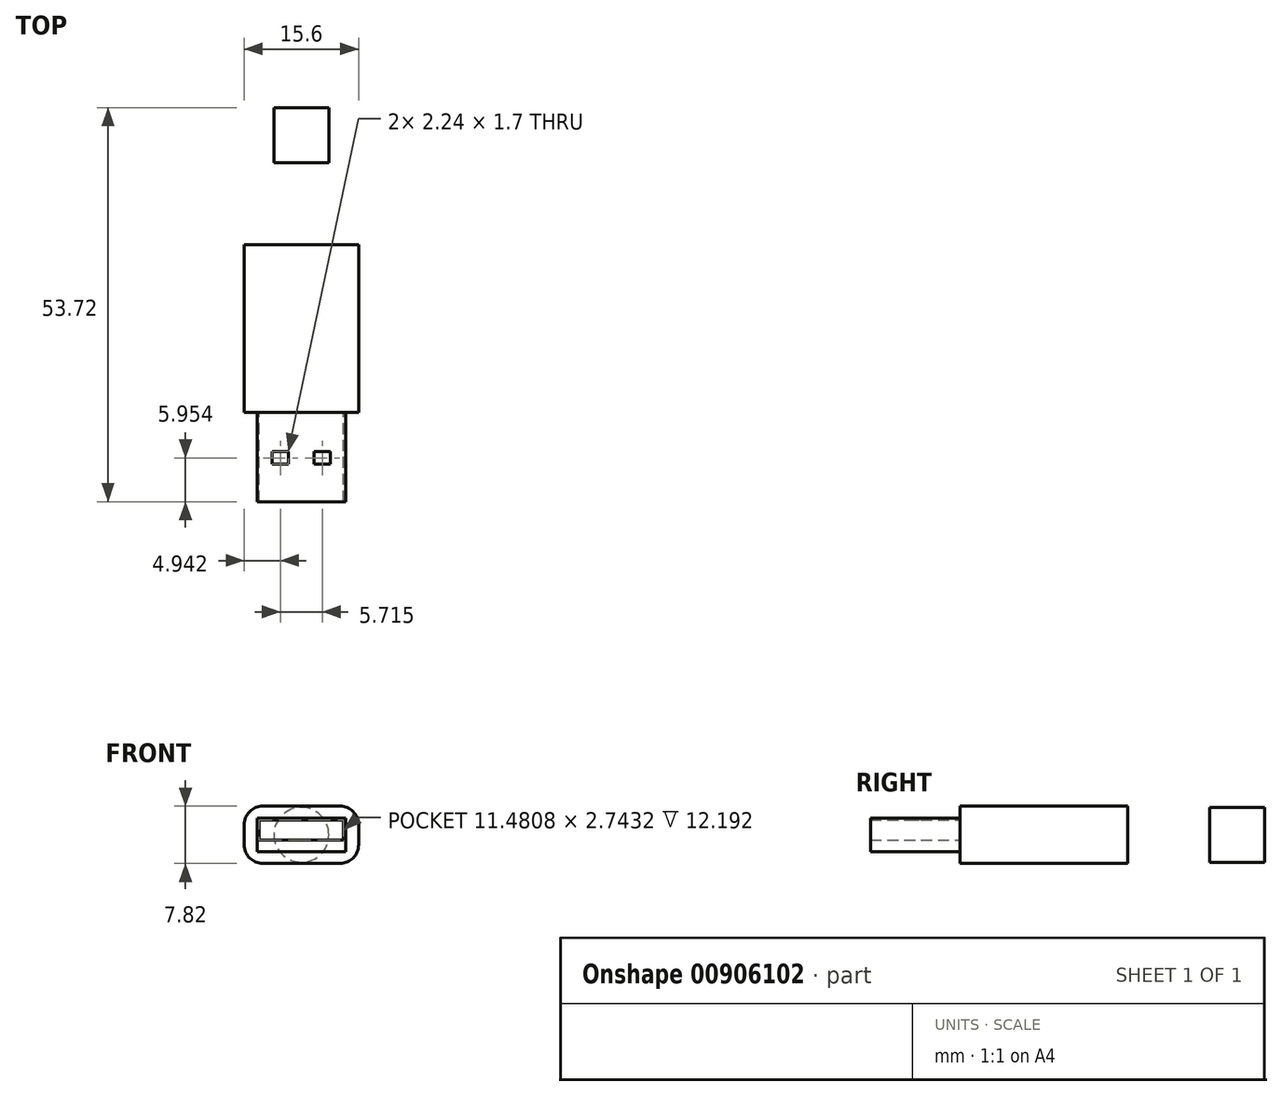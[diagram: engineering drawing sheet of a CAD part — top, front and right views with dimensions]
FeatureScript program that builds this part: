
annotation { "Feature Type Name" : "Feature", "Feature Type Description" : "" }
export const myFeature = defineFeature(function(context is Context, id is Id, definition is map)
    precondition{}
    {
        {
            var Q0;
            Q0=qCreatedBy(makeId("Front.planeOp"),FACE);
            var sketch = newSketch(context, id + "F0", { "sketchPlane" : qUnion([Q0])});
            skLineSegment(sketch, "E0.bottom", {"start": v(6.02, -2.29) * mm, "end": v(-6.02, -2.29) * mm});
            skLineSegment(sketch, "E0.top", {"start": v(6.02, 2.29) * mm, "end": v(-6.02, 2.29) * mm});
            skLineSegment(sketch, "E0.left", {"start": v(6.02, -2.29) * mm, "end": v(6.02, 2.29) * mm});
            skLineSegment(sketch, "E0.right", {"start": v(-6.02, -2.29) * mm, "end": v(-6.02, 2.29) * mm});
            skPoint(sketch, "E0.middle", {"position": v(0, 0) * mm});
            skSolve(sketch);
        }
        {
            var Q0;
            Q0=qSketchRegion(id+"F0",true);
            extrude(context, id + "F1", {"entities" : qUnion([Q0]), "depth" : 12.2 * mm, "offsetDistance" : 25.4 * mm});
        }
        {
            var Q0;
            Q0=makeQuery(id+"F1.opExtrude","CAP_FACE",FACE,{"disambiguationData":[OSD([sQuery(id+"F0.wireOp",EDGE,"E0.bottom"),sQuery(id+"F0.wireOp",EDGE,"E0.top"),sQuery(id+"F0.wireOp",EDGE,"E0.left"),sQuery(id+"F0.wireOp",EDGE,"E0.right")])],"isStart":false});
            var Q1;
            Q1=makeQuery(id+"F1.opExtrude","CAP_FACE",FACE,{"disambiguationData":[OSD([sQuery(id+"F0.wireOp",EDGE,"E0.bottom"),sQuery(id+"F0.wireOp",EDGE,"E0.top"),sQuery(id+"F0.wireOp",EDGE,"E0.left"),sQuery(id+"F0.wireOp",EDGE,"E0.right")])],"isStart":true});
            shell(context, id + "F2", {"entities" : qUnion([Q0, Q1]), "thickness" : 0.28 * mm});
        }
        {
            var Q0;
            Q0=qCreatedBy(makeId("Front.planeOp"),FACE);
            var sketch = newSketch(context, id + "F3", { "sketchPlane" : qUnion([Q0])});
            skLineSegment(sketch, "E1.bottom", {"start": v(5.26, 3.91) * mm, "end": v(-5.26, 3.91) * mm});
            skLineSegment(sketch, "E1.top", {"start": v(5.26, -3.91) * mm, "end": v(-5.26, -3.91) * mm});
            skLineSegment(sketch, "E1.left", {"start": v(7.8, 1.37) * mm, "end": v(7.8, -1.37) * mm});
            skLineSegment(sketch, "E1.right", {"start": v(-7.8, 1.37) * mm, "end": v(-7.8, -1.37) * mm});
            skPoint(sketch, "E1.middle", {"position": v(0, 0) * mm});
            skPoint(sketch, "E2.visualSharp", {"position": v(-7.8, 3.91) * mm});
            skArc(sketch, "E2.filletArc", {"start": v(-5.26, 3.91) * mm, "mid": v(-7.05, 3.17) * mm, "end": v(-7.8, 1.37) * mm});
            skPoint(sketch, "E3.visualSharp", {"position": v(7.8, 3.91) * mm});
            skArc(sketch, "E3.filletArc", {"start": v(7.8, 1.37) * mm, "mid": v(7.05, 3.17) * mm, "end": v(5.26, 3.91) * mm});
            skPoint(sketch, "E4.visualSharp", {"position": v(7.8, -3.91) * mm});
            skArc(sketch, "E4.filletArc", {"start": v(5.26, -3.91) * mm, "mid": v(7.05, -3.17) * mm, "end": v(7.8, -1.37) * mm});
            skPoint(sketch, "E5.visualSharp", {"position": v(-7.8, -3.91) * mm});
            skArc(sketch, "E5.filletArc", {"start": v(-7.8, -1.37) * mm, "mid": v(-7.05, -3.17) * mm, "end": v(-5.26, -3.91) * mm});
            skSolve(sketch);
        }
        {
            var Q0;
            Q0=qSketchRegion(id+"F3",true);
            extrude(context, id + "F4", {"entities" : qUnion([Q0]), "operationType" : NewBodyOperationType.ADD, "oppositeDirection" : true, "depth" : 22.86 * mm, "offsetDistance" : 25.4 * mm});
        }
        {
            var Q0;
            Q0=makeQuery(id+"F2.opShell","OFFSET_FACE",FACE,{"disambiguationData":[OSD([sQuery(id+"F0.wireOp",EDGE,"E0.bottom")])]});
            var sketch = newSketch(context, id + "F5", { "sketchPlane" : qUnion([Q0])});
            skLineSegment(sketch, "E6.0", {"start": v(-5.74, -12.2) * mm, "end": v(-5.74, 0) * mm});
            skLineSegment(sketch, "E6.1", {"start": v(5.74, 0) * mm, "end": v(-5.74, 0) * mm});
            skLineSegment(sketch, "E6.2", {"start": v(5.74, -12.2) * mm, "end": v(5.74, 0) * mm});
            skLineSegment(sketch, "E6.3", {"start": v(5.74, -12.2) * mm, "end": v(-5.74, -12.2) * mm});
            skSolve(sketch);
        }
        {
            var Q0;
            Q0=makeQuery(id+"F5.imprint","IMPRINT",FACE,{"disambiguationData":[TD([[makeQuery(id+"F5.imprint","IMPRINT",EDGE,{"derivedFrom":sQuery(id+"F5.wireOp",EDGE,"E6.0")}),-1.0]])]});
            extrude(context, id + "F6", {"entities" : qUnion([Q0]), "operationType" : NewBodyOperationType.ADD, "depth" : 1.27 * mm, "offsetDistance" : 25.4 * mm});
        }
        {
            var Q0;
            Q0=makeQuery(id+"F1.opExtrude","SWEPT_FACE",FACE,{"disambiguationData":[OSD([sQuery(id+"F0.wireOp",EDGE,"E0.top")])]});
            var sketch = newSketch(context, id + "F7", { "sketchPlane" : qUnion([Q0])});
            skLineSegment(sketch, "E7.bottom", {"start": v(-1.74, -7.09) * mm, "end": v(-3.98, -7.09) * mm});
            skLineSegment(sketch, "E7.top", {"start": v(-1.74, -5.38) * mm, "end": v(-3.98, -5.38) * mm});
            skLineSegment(sketch, "E7.left", {"start": v(-1.74, -7.09) * mm, "end": v(-1.74, -5.38) * mm});
            skLineSegment(sketch, "E7.right", {"start": v(-3.98, -7.09) * mm, "end": v(-3.98, -5.38) * mm});
            skPoint(sketch, "E7.middle", {"position": v(-2.86, -6.24) * mm});
            skLineSegment(sketch, "E8.bottom", {"start": v(3.98, -7.09) * mm, "end": v(1.74, -7.09) * mm});
            skLineSegment(sketch, "E8.top", {"start": v(3.98, -5.38) * mm, "end": v(1.74, -5.38) * mm});
            skLineSegment(sketch, "E8.left", {"start": v(3.98, -7.09) * mm, "end": v(3.98, -5.38) * mm});
            skLineSegment(sketch, "E8.right", {"start": v(1.74, -7.09) * mm, "end": v(1.74, -5.38) * mm});
            skPoint(sketch, "E8.middle", {"position": v(2.86, -6.24) * mm});
            skLineSegment(sketch, "E9", {"start": v(0, 0) * mm, "end": v(0, -12.2) * mm, "construction": true});
            skSolve(sketch);
        }
        {
            var Q0;
            Q0=qSketchRegion(id+"F7",true);
            extrude(context, id + "F8", {"entities" : qUnion([Q0]), "operationType" : NewBodyOperationType.REMOVE, "endBound" : BoundingType.UP_TO_NEXT, "oppositeDirection" : true, "depth" : 25.4 * mm, "offsetDistance" : 25.4 * mm});
        }
        {
            var Q0;
            {var subQ0=sQuery(id+"F3.wireOp",EDGE,"E3.filletArc");var subQ1=sQuery(id+"F3.wireOp",EDGE,"E1.right");var subQ2=sQuery(id+"F3.wireOp",EDGE,"E1.left");var subQ3=sQuery(id+"F3.wireOp",EDGE,"E1.top");var subQ4=sQuery(id+"F3.wireOp",EDGE,"E2.filletArc");var subQ5=sQuery(id+"F3.wireOp",EDGE,"E1.bottom");var subQ6=sQuery(id+"F3.wireOp",EDGE,"E4.filletArc");var subQ7=sQuery(id+"F3.wireOp",EDGE,"E5.filletArc");Q0=makeQuery(id+"F4.boolean.opBoolean","SPLIT",FACE,{"disambiguationData":[TD([makeQuery(id+"F1.opExtrude","SWEPT_FACE",FACE,{"disambiguationData":[OSD([sQuery(id+"F0.wireOp",EDGE,"E0.bottom")])]})])],"derivedFrom":makeQuery(id+"F4.opExtrude","CAP_FACE",FACE,{"disambiguationData":[OSD([subQ5,subQ3,subQ2,subQ1,subQ4,subQ0,subQ6,subQ7])],"isStart":true})});}
            cPlane(context, id + "F9", {"entities" : qUnion([Q0]), "cplaneType" : CPlaneType.OFFSET, "offset" : 41.53 * mm, "oppositeDirection" : true, "width" : 152.4 * mm, "height" : 152.4 * mm});
        }
        {
            var Q0;
            Q0=qCreatedBy(id+"F9.planeOp",FACE);
            var sketch = newSketch(context, id + "F10", { "sketchPlane" : qUnion([Q0])});
            skCircle(sketch, "E10", {"center": v(0, 0) * mm, "radius": 3.75 * mm});
            skSolve(sketch);
        }
        {
            var Q0;
            Q0=makeQuery(id+"F10.imprint","IMPRINT",FACE,{"disambiguationData":[TD([[makeQuery(id+"F10.imprint","IMPRINT",EDGE,{"derivedFrom":sQuery(id+"F10.wireOp",EDGE,"E10")}),1.0]])]});
            extrude(context, id + "F11", {"entities" : qUnion([Q0]), "depth" : 7.5 * mm, "offsetDistance" : 25.4 * mm});
        }
    });
